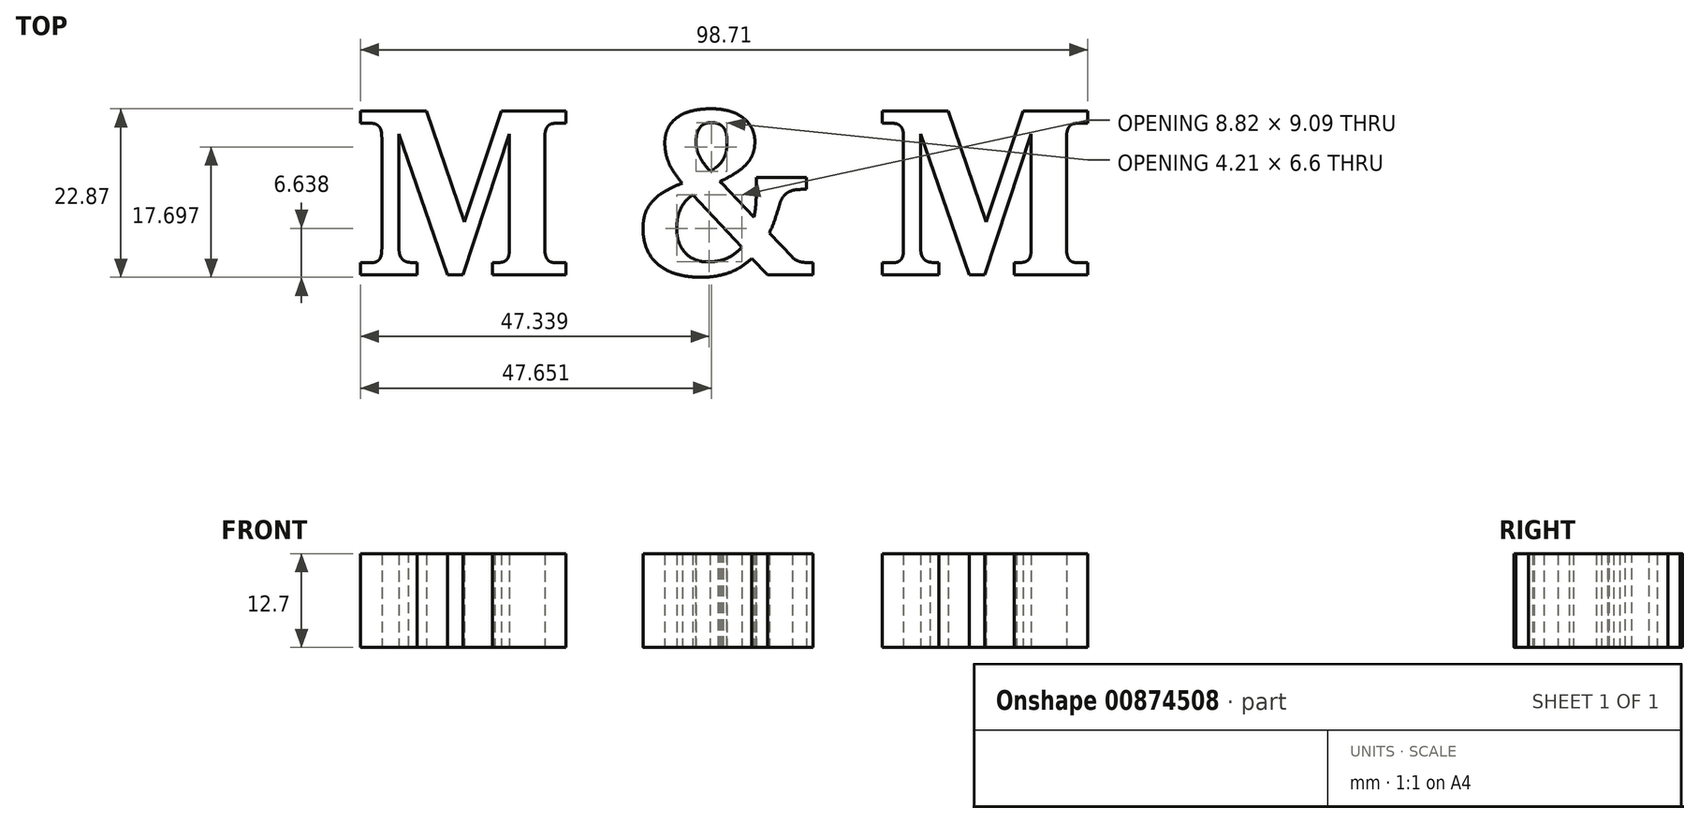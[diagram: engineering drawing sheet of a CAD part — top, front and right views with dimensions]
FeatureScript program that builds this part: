
annotation { "Feature Type Name" : "Feature", "Feature Type Description" : "" }
export const myFeature = defineFeature(function(context is Context, id is Id, definition is map)
    precondition{}
    {
        {
            var Q0;
            Q0=qCreatedBy(makeId("Top.planeOp"),FACE);
            var sketch = newSketch(context, id + "F0", { "sketchPlane" : qUnion([Q0])});
            skText(sketch, "E0", { "text": "M & M", "fontName": "NotoSerif-Bold.ttf"});
            const initialGuessF0  = {"E0": [-0.03079, 0.00126, 1, 0, 0.02243]};
            skSetInitialGuess(sketch, initialGuessF0);
            skSolve(sketch);
        }
        {
            var Q0;
            Q0 = qSketchRegion(id + "F0", true);
            extrude(context, id + "F1", {"entities" : qUnion([Q0]), "depth" : 12.7 * mm, "offsetDistance" : 25.4 * mm});
        }
    });
